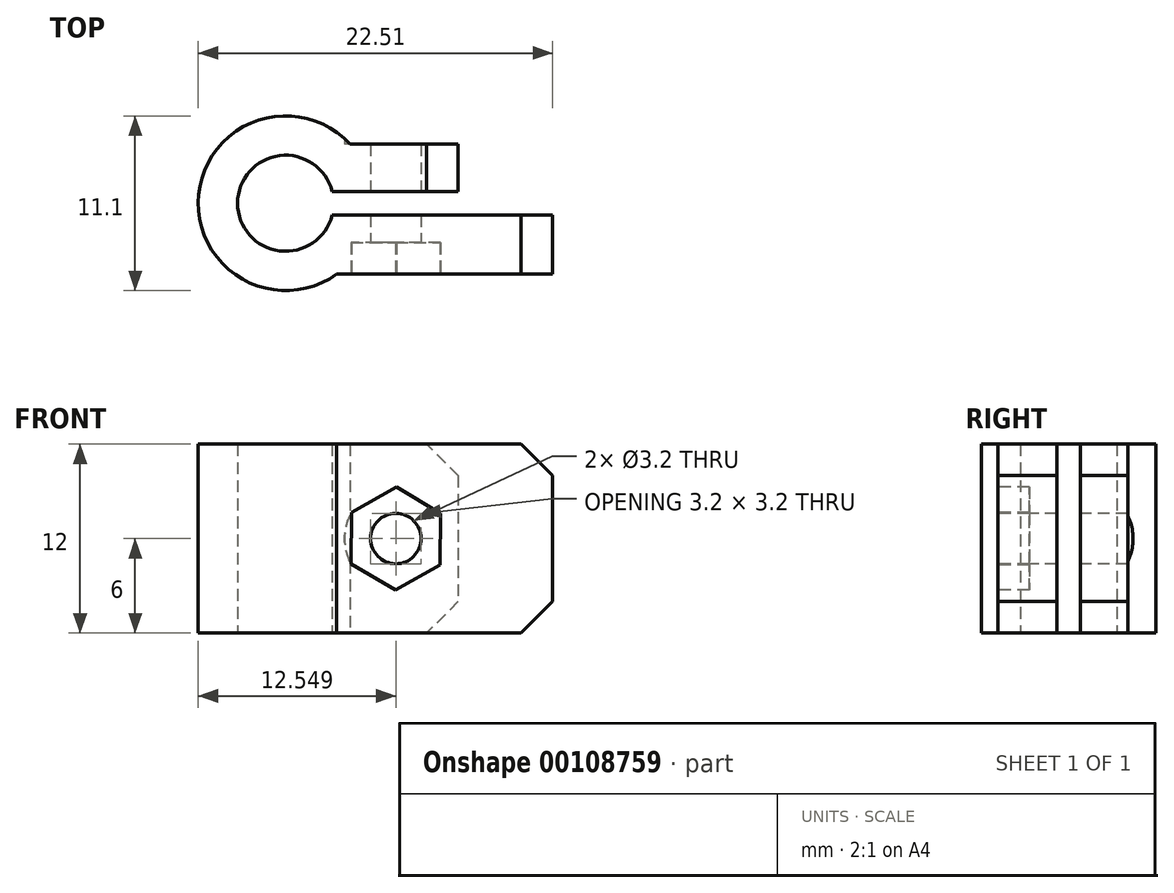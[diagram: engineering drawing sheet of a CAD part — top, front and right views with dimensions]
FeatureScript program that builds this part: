
annotation { "Feature Type Name" : "Feature", "Feature Type Description" : "" }
export const myFeature = defineFeature(function(context is Context, id is Id, definition is map)
    precondition{}
    {
        {
            var Q0;
            Q0=qCreatedBy(makeId("Top.planeOp"),FACE);
            var sketch = newSketch(context, id + "F0", { "sketchPlane" : qUnion([Q0])});
            skArc(sketch, "E0", {"start": v(2.96, 0.75) * mm, "mid": v(-3.05, 0) * mm, "end": v(2.96, -0.75) * mm});
            skArc(sketch, "E1", {"start": v(4.1, 3.75) * mm, "mid": v(-5.52, 0.56) * mm, "end": v(3.25, -4.5) * mm});
            skLineSegment(sketch, "E2", {"start": v(2.96, 0.75) * mm, "end": v(10.96, 0.75) * mm});
            skLineSegment(sketch, "E3", {"start": v(10.96, 0.75) * mm, "end": v(10.96, 3.75) * mm});
            skLineSegment(sketch, "E4", {"start": v(10.96, 3.75) * mm, "end": v(4.1, 3.75) * mm});
            skLineSegment(sketch, "E5", {"start": v(2.96, -0.75) * mm, "end": v(16.96, -0.75) * mm});
            skLineSegment(sketch, "E6", {"start": v(16.96, -0.75) * mm, "end": v(16.96, -4.5) * mm});
            skLineSegment(sketch, "E7", {"start": v(16.96, -4.5) * mm, "end": v(3.25, -4.5) * mm});
            skSolve(sketch);
        }
        {
            var Q0;
            Q0=makeQuery(id+"F0.imprint","IMPRINT",FACE,{"disambiguationData":[TD([[makeQuery(id+"F0.imprint","IMPRINT",EDGE,{"derivedFrom":sQuery(id+"F0.wireOp",EDGE,"E0")}),-1.0]])]});
            extrude(context, id + "F1", {"entities" : qUnion([Q0]), "depth" : 12 * mm});
        }
        {
            var Q0;
            Q0=makeQuery(id+"F1.opExtrude","SWEPT_FACE",FACE,{"disambiguationData":[OSD([sQuery(id+"F0.wireOp",EDGE,"E7")])]});
            var sketch = newSketch(context, id + "F2", { "sketchPlane" : qUnion([Q0])});
            skLineSegment(sketch, "E8", {"start": v(3.25, 6) * mm, "end": v(16.96, 6) * mm, "construction": true});
            skCircle(sketch, "E9.cCircle", {"center": v(7, 6) * mm, "radius": 2.84 * mm, "construction": true});
            skLineSegment(sketch, "E9.0", {"start": v(7.03, 9.28) * mm, "end": v(9.85, 7.61) * mm});
            skLineSegment(sketch, "E9.1", {"start": v(9.85, 7.61) * mm, "end": v(9.82, 4.33) * mm});
            skLineSegment(sketch, "E9.2", {"start": v(9.82, 4.33) * mm, "end": v(6.97, 2.72) * mm});
            skLineSegment(sketch, "E9.3", {"start": v(6.97, 2.72) * mm, "end": v(4.15, 4.39) * mm});
            skLineSegment(sketch, "E9.4", {"start": v(4.15, 4.39) * mm, "end": v(4.18, 7.67) * mm});
            skLineSegment(sketch, "E9.5", {"start": v(4.18, 7.67) * mm, "end": v(7.03, 9.28) * mm});
            skPoint(sketch, "E9.0.midPoint", {"position": v(8.44, 8.44) * mm});
            skCircle(sketch, "E10", {"center": v(7, 6) * mm, "radius": 1.6 * mm});
            skSolve(sketch);
        }
        {
            var Q0;
            Q0=makeQuery(id+"F2.imprint","IMPRINT",FACE,{"disambiguationData":[TD([[makeQuery(id+"F2.imprint","IMPRINT",EDGE,{"derivedFrom":sQuery(id+"F2.wireOp",EDGE,"E9.0")}),-1.0]])]});
            var Q1;
            Q1=makeQuery(id+"F2.imprint","IMPRINT",FACE,{"disambiguationData":[TD([[makeQuery(id+"F2.imprint","IMPRINT",EDGE,{"derivedFrom":sQuery(id+"F2.wireOp",EDGE,"E10")}),1.0]])]});
            extrude(context, id + "F3", {"entities" : qUnion([Q0, Q1]), "operationType" : NewBodyOperationType.REMOVE, "oppositeDirection" : true, "depth" : 2 * mm});
        }
        {
            var Q0;
            Q0=makeQuery(id+"F2.imprint","IMPRINT",FACE,{"disambiguationData":[TD([[makeQuery(id+"F2.imprint","IMPRINT",EDGE,{"derivedFrom":sQuery(id+"F2.wireOp",EDGE,"E10")}),1.0]])]});
            extrude(context, id + "F4", {"entities" : qUnion([Q0]), "operationType" : NewBodyOperationType.REMOVE, "endBound" : BoundingType.THROUGH_ALL, "oppositeDirection" : true, "depth" : 25 * mm});
        }
        {
            var Q0;
            Q0=makeQuery(id+"F1.opExtrude","SWEPT_FACE",FACE,{"disambiguationData":[OSD([sQuery(id+"F0.wireOp",EDGE,"E4")])]});
            var sketch = newSketch(context, id + "F5", { "sketchPlane" : qUnion([Q0])});
            skCircle(sketch, "E11", {"center": v(-7, 6) * mm, "radius": 3.25 * mm});
            skSolve(sketch);
        }
        {
            var Q0;
            {var subQ1=sQuery(id+"F0.wireOp",EDGE,"E4");Q0=makeQuery(id+"F5.imprint","IMPRINT",FACE,{"disambiguationData":[TD([[makeQuery(id+"F5.imprint","IMPRINT",EDGE,{"derivedFrom":makeQuery(id+"F4.boolean.opBoolean","INTERSECT",EDGE,{"derivedFrom":[makeQuery(id+"F1.opExtrude","SWEPT_FACE",FACE,{"disambiguationData":[OSD([subQ1])]}),makeQuery(id+"F4.opExtrude","SWEPT_FACE",FACE,{"disambiguationData":[OSD([sQuery(id+"F2.wireOp",EDGE,"E10")])]})]})}),1.0]])]});}
            var Q1;
            {var subQ0=sQuery(id+"F5.wireOp",EDGE,"E11");var subQ1=makeQuery(id+"F1.opExtrude","SWEPT_EDGE",EDGE,{"disambiguationData":[OSD([sQuery(id+"F0.wireOp",EDGE,"E1"),sQuery(id+"F0.wireOp",EDGE,"E4")])]});var subQ2=makeQuery(id+"F5.imprint","INTERSECT",VERTEX,{"disambiguationData":[OD(0.0)],"derivedFrom":[subQ1,subQ0]});Q1=makeQuery(id+"F5.imprint","IMPRINT",FACE,{"disambiguationData":[TD([[makeQuery(id+"F5.imprint","IMPRINT",EDGE,{"disambiguationData":[TD([[subQ2,-1.0]])],"derivedFrom":subQ0}),1.0]])]});}
            extrude(context, id + "F6", {"entities" : qUnion([Q0, Q1]), "operationType" : NewBodyOperationType.REMOVE, "depth" : 25 * mm});
        }
        {
            var Q0;
            Q0=makeQuery(id+"F1.opExtrude","CAP_EDGE",EDGE,{"disambiguationData":[OSD([sQuery(id+"F0.wireOp",EDGE,"E6")])],"isStart":false});
            var Q1;
            Q1=makeQuery(id+"F1.opExtrude","CAP_EDGE",EDGE,{"disambiguationData":[OSD([sQuery(id+"F0.wireOp",EDGE,"E6")])],"isStart":true});
            var Q2;
            Q2=makeQuery(id+"F1.opExtrude","CAP_EDGE",EDGE,{"disambiguationData":[OSD([sQuery(id+"F0.wireOp",EDGE,"E3")])],"isStart":true});
            var Q3;
            Q3=makeQuery(id+"F1.opExtrude","CAP_EDGE",EDGE,{"disambiguationData":[OSD([sQuery(id+"F0.wireOp",EDGE,"E3")])],"isStart":false});
            chamfer(context, id + "F7", {"entities" : qUnion([Q0, Q1, Q2, Q3]), "width" : 2 * mm, "tangentPropagation" : true});
        }
    });
